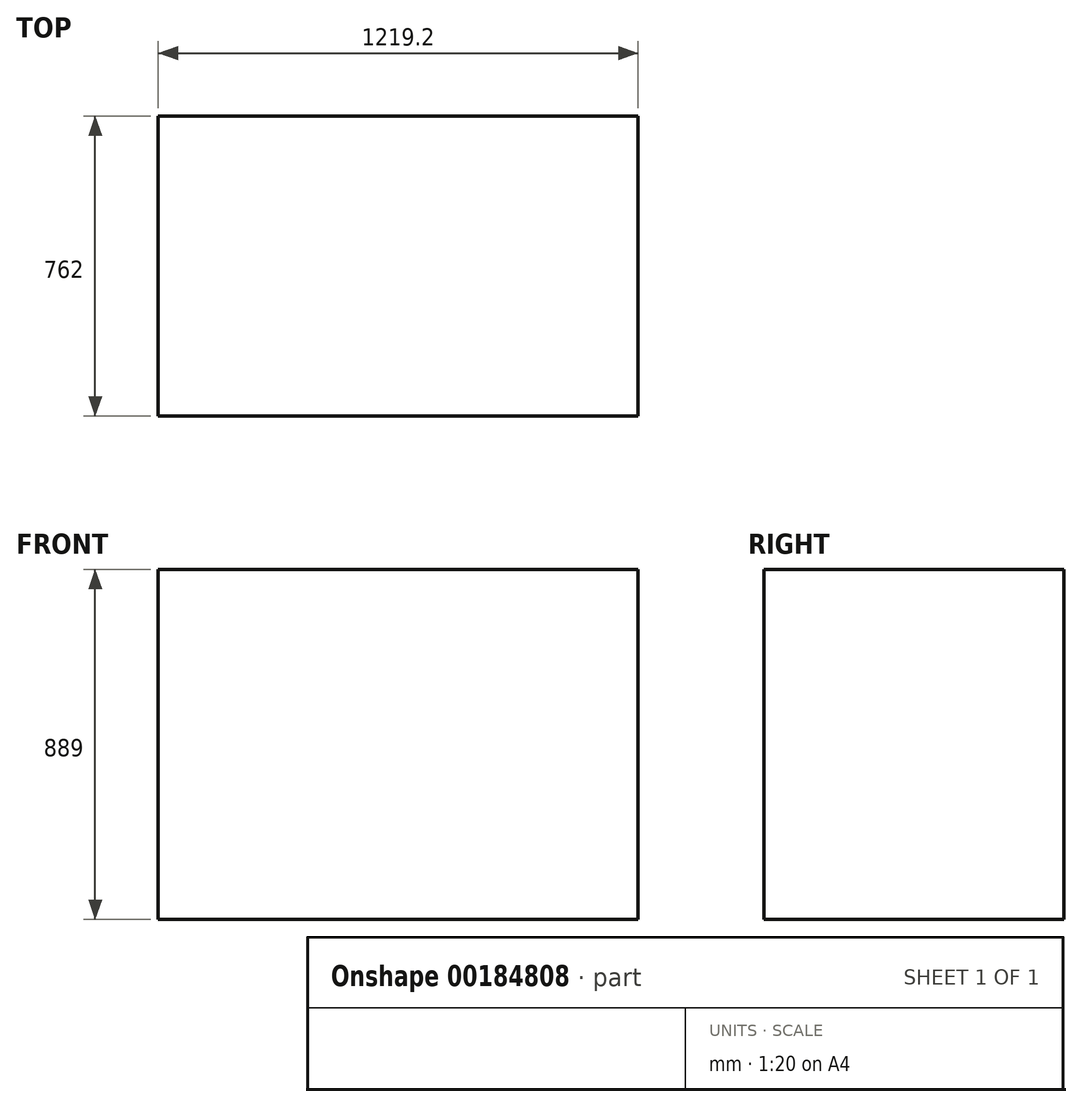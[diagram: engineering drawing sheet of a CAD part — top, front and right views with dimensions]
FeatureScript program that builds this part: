
annotation { "Feature Type Name" : "Feature", "Feature Type Description" : "" }
export const myFeature = defineFeature(function(context is Context, id is Id, definition is map)
    precondition{}
    {
        {
            var Q0;
            Q0=qCreatedBy(makeId("Top.planeOp"),FACE);
            var sketch = newSketch(context, id + "F0", { "sketchPlane" : qUnion([Q0])});
            skLineSegment(sketch, "E0.bottom", {"start": v(609.6, -381) * mm, "end": v(-609.6, -381) * mm});
            skLineSegment(sketch, "E0.top", {"start": v(609.6, 381) * mm, "end": v(-609.6, 381) * mm});
            skLineSegment(sketch, "E0.left", {"start": v(609.6, -381) * mm, "end": v(609.6, 381) * mm});
            skLineSegment(sketch, "E0.right", {"start": v(-609.6, -381) * mm, "end": v(-609.6, 381) * mm});
            skPoint(sketch, "E0.middle", {"position": v(0, 0) * mm});
            skSolve(sketch);
        }
        {
            var Q0;
            Q0 = qSketchRegion(id + "F0", true);
            var Q1;
            Q1=makeQuery(id+"F0.imprint","IMPRINT",FACE,{"disambiguationData":[TD([[makeQuery(id+"F0.imprint","IMPRINT",EDGE,{"derivedFrom":sQuery(id+"F0.wireOp",EDGE,"E0.bottom")}),-1.0]])]});
            extrude(context, id + "F1", {"entities" : qUnion([Q0, Q1]), "depth" : 889 * mm});
        }
    });
